# Revit family: DC_Rheem_PLM_ HeavyDutyElectric_50L
name_source: partatom
category: Plumbing Fixtures
units: mm (PartAtom-declared; Revit-internal decimal feet)

## family parameters
Cut with Voids When Loaded = No
Host = Face
Part Type = Normal
Room Calculation Point = No
Round Connector Dimension = Use Radius
Shared = No

## types (2) — shared parameters
ColdWaterInletHeight_ANZRS = 98 mm
ColdWaterPipeRadius_ANZRS = 1"
Diameter_ANZRS = 436 mm
H1_ANZRS = 475 mm
H_ANZRS = 74 mm
Height_ANZRS = 660 mm
HotWaterOutletHeight_ANZRS = 405 mm
HotWaterPipeRadius_ANZRS = 1"
L1_ANZRS = 264 mm
Manufacturer = Rheem
Materials_ANZRS = Rheem - Joey Grey Steel
Radius_ANZRS = 218 mm
T&PRValveConnection_ANZRS = 0"
Type Comments = 240L first hour delivery @ 50°C rise
URL = http://www.rheem.com.au
zero-valued in all types: Default Elevation

## per-type parameters (varying)
| type | Model |
| Heavy Duty Electric Storage - Indoor/Outdoor - 50L - 3 x 3.6kW | 61305007 |
| Heavy Duty Electric Storage - Indoor/Outdoor - 50L - 3 x 4.8kW | 61305008 |

note: column(s) folded — value = type name in every type: Description

## geometry (parser evidence)
native form markers: Sweep x2
no freeform markers — native parametric forms only
